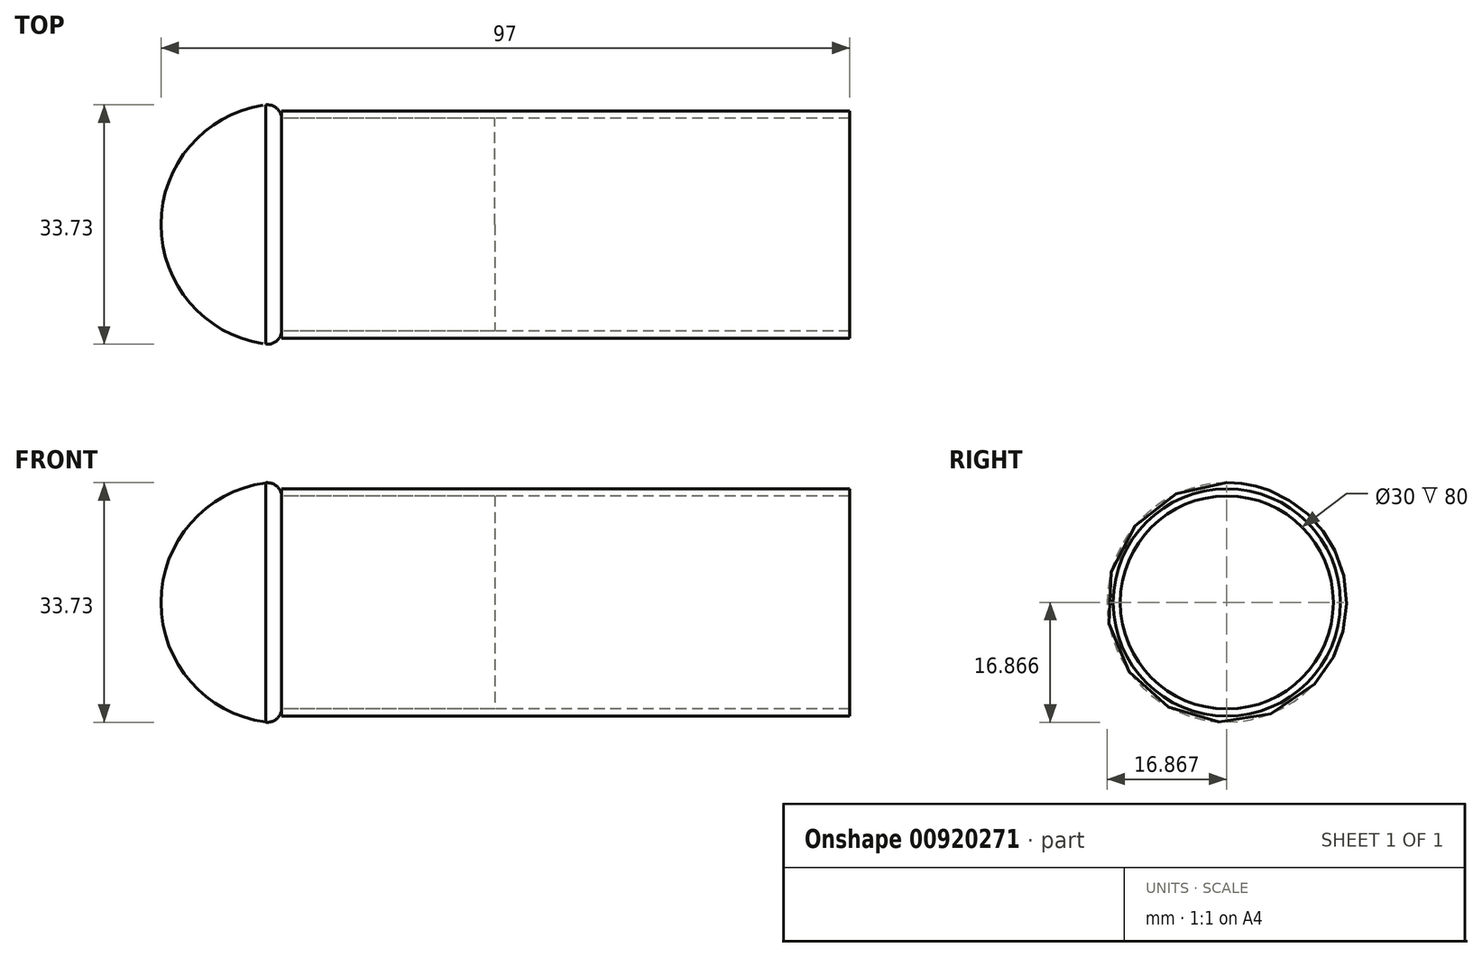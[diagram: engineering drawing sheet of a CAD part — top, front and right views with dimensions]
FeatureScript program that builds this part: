
annotation { "Feature Type Name" : "Feature", "Feature Type Description" : "" }
export const myFeature = defineFeature(function(context is Context, id is Id, definition is map)
    precondition{}
    {
        {
            var Q0;
            Q0=qCreatedBy(makeId("Right.planeOp"),FACE);
            var sketch = newSketch(context, id + "F0", { "sketchPlane" : qUnion([Q0])});
            skLineSegment(sketch, "E0", {"start": v(-3.95, -7.37) * mm, "end": v(30.05, -7.37) * mm});
            skArc(sketch, "E1", {"start": v(-3.95, -7.37) * mm, "mid": v(13.05, -24.37) * mm, "end": v(30.05, -7.37) * mm});
            skSolve(sketch);
        }
        {
            var Q0;
            Q0=makeQuery(id+"F0.imprint","IMPRINT",FACE,{"disambiguationData":[TD([[makeQuery(id+"F0.imprint","IMPRINT",EDGE,{"derivedFrom":sQuery(id+"F0.wireOp",EDGE,"E0")}),-1.0]])]});
            var Q1;
            Q1=sQuery(id+"F0.wireOp",EDGE,"E0");
            revolve(context, id + "F1", {"entities" : qUnion([Q0]), "axis" : qUnion([Q1]), "revolveType" : RevolveType.ONE_DIRECTION, "angle" : 180 * degree});
        }
        {
            var Q0;
            Q0=makeQuery(id+"F1.opRevolve","CAP_FACE",FACE,{"disambiguationData":[OSD([sQuery(id+"F0.wireOp",EDGE,"E0"),sQuery(id+"F0.wireOp",EDGE,"E1")])],"isStart":true});
            var sketch = newSketch(context, id + "F2", { "sketchPlane" : qUnion([Q0])});
            skCircle(sketch, "E2", {"center": v(13.05, -7.37) * mm, "radius": 15 * mm});
            skSolve(sketch);
        }
        {
            var Q0;
            Q0=makeQuery(id+"F2.imprint","IMPRINT",FACE,{"disambiguationData":[TD([[makeQuery(id+"F2.imprint","IMPRINT",EDGE,{"derivedFrom":sQuery(id+"F2.wireOp",EDGE,"E2")}),1.0]])]});
            extrude(context, id + "F3", {"entities" : qUnion([Q0]), "operationType" : NewBodyOperationType.ADD, "depth" : 30 * mm});
        }
        {
            var Q0;
            Q0=makeQuery(id+"F1.opRevolve","CAP_FACE",FACE,{"disambiguationData":[OSD([sQuery(id+"F0.wireOp",EDGE,"E0"),sQuery(id+"F0.wireOp",EDGE,"E1")])],"isStart":true});
            var sketch = newSketch(context, id + "F4", { "sketchPlane" : qUnion([Q0])});
            skCircle(sketch, "E3.0", {"center": v(13.05, -7.37) * mm, "radius": 15 * mm});
            skCircle(sketch, "E4", {"center": v(13.05, -7.37) * mm, "radius": 16 * mm});
            skSolve(sketch);
        }
        {
            var Q0;
            Q0=makeQuery(id+"F4.imprint","IMPRINT",FACE,{"disambiguationData":[TD([[makeQuery(id+"F4.imprint","IMPRINT",EDGE,{"derivedFrom":sQuery(id+"F4.wireOp",EDGE,"E3.0")}),-1.0]])]});
            extrude(context, id + "F5", {"entities" : qUnion([Q0]), "depth" : 80 * mm});
        }
        {
            var Q0;
            Q0=makeQuery(id+"F1.opRevolve","CAP_EDGE",EDGE,{"disambiguationData":[OSD([sQuery(id+"F0.wireOp",EDGE,"E1")])],"isStart":true});
            fillet(context, id + "F6", {"entities" : qUnion([Q0]), "radius" : 2 * mm, "tangentPropagation" : true, "allowEdgeOverflow" : false});
        }
    });
